# Revit family: WA-Panel
name_source: partatom
category: Generic Models
revit_build: Autodesk Revit Architecture 2012 (Build: 20110916_2132(x64)
units: mm (PartAtom-declared; Revit-internal decimal feet)

## types (15) — shared parameters
Description = Acoustic Panel
Keynote = Acoustic Wall Absorber Panels
Manufacturer = Wenger Corporation
Part Number = 161G115
Thickness = 2 7/8"
Type Comments = Rectangular
URL = http://www.wengercorp.com

## per-type parameters (varying)
| type | Height | Width |
| 2'x2' | 23 3/16" | 23 3/16" |
| 2'x3' | 35 3/16" | 23 3/16" |
| 2'x4' | 46 7/8" | 23 3/16" |
| 2'x5' | 59 7/8" | 23 3/16" |
| 2'x6' | 70 7/8" | 23 3/16" |
| 2'x8' | 94 7/8" | 23 3/16" |
| 3'x3' | 35 3/16" | 35 3/16" |
| 3'x4' | 46 7/8" | 35 3/16" |
| 3'x5' | 58 7/8" | 35 3/16" |
| 3'x6' | 70 7/8" | 35 3/16" |
| 3'x8' | 94 7/8" | 35 3/16" |
| 4'x4' | 46 7/8" | 46 7/8" |
| 4'x5' | 58 7/8" | 46 7/8" |
| 4'x6' | 70 7/8" | 46 7/8" |
| 4'x8' | 94 7/8" | 46 7/8" |

## geometry (parser evidence)
native form markers: Sweep x3
no freeform markers — native parametric forms only
